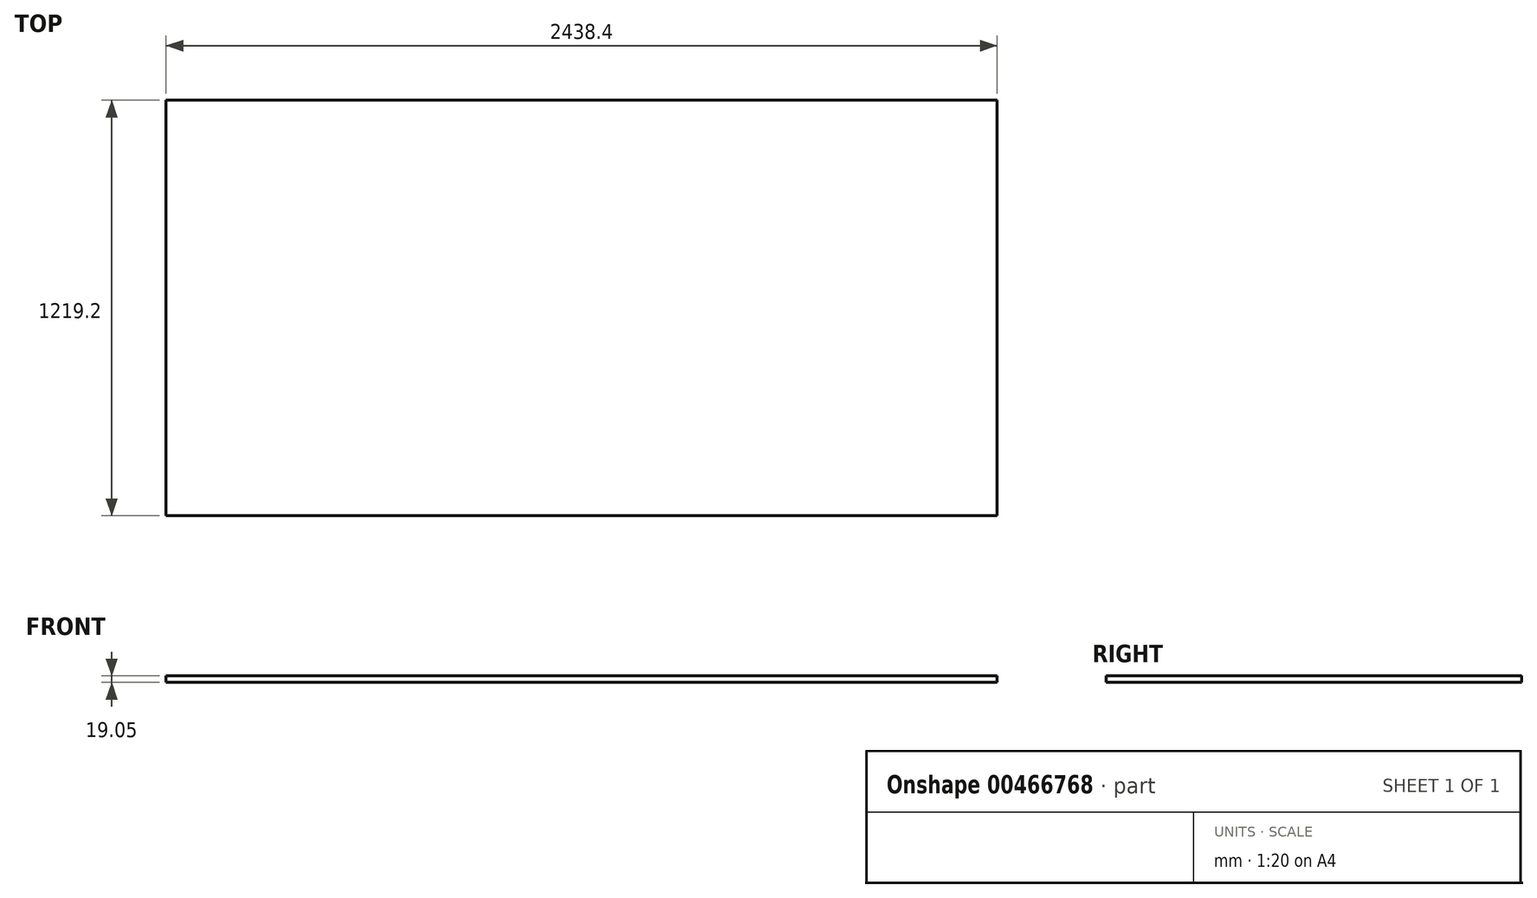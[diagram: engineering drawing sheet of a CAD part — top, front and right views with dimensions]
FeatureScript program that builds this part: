
annotation { "Feature Type Name" : "Feature", "Feature Type Description" : "" }
export const myFeature = defineFeature(function(context is Context, id is Id, definition is map)
    precondition{}
    {
        {
            var Q0;
            Q0=qCreatedBy(makeId("Top.planeOp"),FACE);
            var sketch = newSketch(context, id + "F0", { "sketchPlane" : qUnion([Q0])});
            skLineSegment(sketch, "E0.bottom", {"start": v(1219.2, -609.6) * mm, "end": v(-1219.2, -609.6) * mm});
            skLineSegment(sketch, "E0.top", {"start": v(1219.2, 609.6) * mm, "end": v(-1219.2, 609.6) * mm});
            skLineSegment(sketch, "E0.left", {"start": v(1219.2, -609.6) * mm, "end": v(1219.2, 609.6) * mm});
            skLineSegment(sketch, "E0.right", {"start": v(-1219.2, -609.6) * mm, "end": v(-1219.2, 609.6) * mm});
            skPoint(sketch, "E0.middle", {"position": v(0, 0) * mm});
            skSolve(sketch);
        }
        {
            var Q0;
            Q0 = qSketchRegion(id + "F0", true);
            extrude(context, id + "F1", {"entities" : qUnion([Q0]), "depth" : 19.05 * mm});
        }
    });
